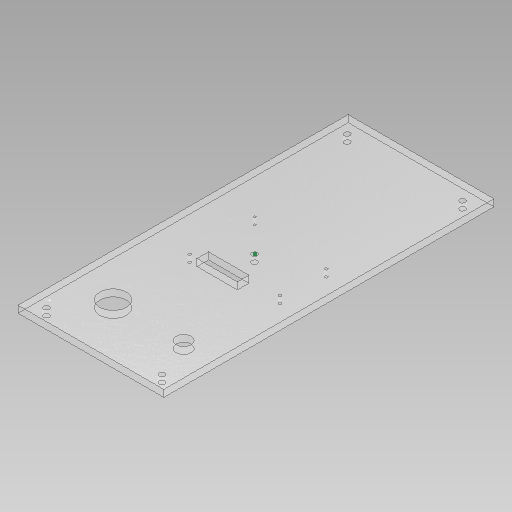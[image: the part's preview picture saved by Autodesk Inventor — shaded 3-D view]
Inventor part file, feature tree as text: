
AUTODESK INVENTOR PART (.ipt)
format: ipt  version: 2020 (Build 240168000, 168)  size: 204,800 bytes
history: native  units: in
note: dims shown in document units (in); Inventor stores cm internally (conversion verified against a paired STEP export)
features: sketch x5, extrude x4
ambient origin geometry x8: Origin, YZ Plane, XZ Plane, XY Plane, X Axis, Y Axis, Z Axis, Center Point
bodies: Solid1 (feature_tree)
feature tree (9):
  extrude  "Extrusion1"  Depth=10.2362in
  extrude  "Extrusion2"  Depth=10.8268in
  sketch  "Sketch3"  dims[d4=0.1969in d5=0.1969in]
  extrude  "Extrusion3"  Depth=0.1969in
  extrude  "Extrusion4"  Depth=0.1969in
  sketch  "Sketch1"  dims[d0=3.937in d1=10.2362in]
  sketch  "Sketch2"  dims[d2=4.5276in d3=10.8268in]
  sketch  "Sketch4"  dims[d6=0.1969in d7=0.1969in]
  sketch  "Sketch5"  dims[d8=0.2362in d9=0.0in d10=0.1969in d11=1.6535in d12=1.6535in d13=1.1024in d14=1.1024in d15=2.2047in d16=0.7874in d17=1.5748in d18=0.0984in d19=0.0787in d20=0.0984in d21=0.0984in d22=0.1969in d23=0.1969in d24=0.1969in d25=1.378in d26=0.2362in d27=0.0in d28=0.9055in d29=0.5118in d30=0.3937in d31=0.0in d32=0.2598in d33=0.2598in d34=0.2953in d35=0.1772in d36=0.1181in d37=0.2362in d38=0.0in]
